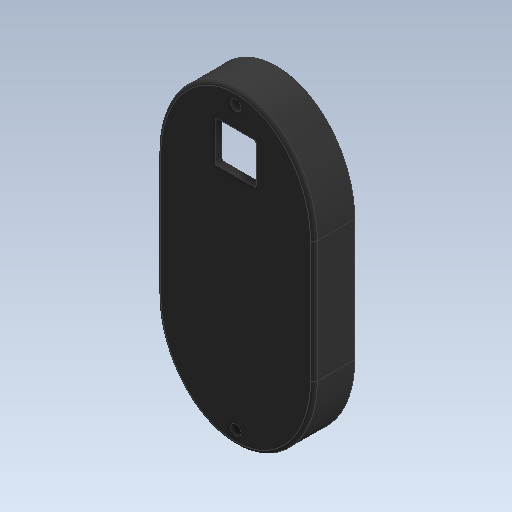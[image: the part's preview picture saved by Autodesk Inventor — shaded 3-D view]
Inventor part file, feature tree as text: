
AUTODESK INVENTOR PART (.ipt)
format: ipt  version: 2020 (Build 240168000, 168)  size: 245,760 bytes
history: native  units: mm
features: sketch x6, extrude x5, other x3, fillet x2, reference x2, projected_geometry x2, hole x1
ambient origin geometry x8: Origin, YZ Plane, XZ Plane, XY Plane, X Axis, Y Axis, Z Axis, Center Point
bodies: Solid1 (feature_tree)
feature tree (21):
  extrude  "Extrusion1"  Depth=10.0mm
  extrude  "Extrusion2"  Depth=10.0mm TaperAngle=0.0deg
  extrude  "Extrusion3"  Depth=8.0mm
  extrude  "Extrusion4"  Depth=10.0mm
  fillet  "Fillet1"  Radius=12.0mm
  hole  "Hole1"  [1 undecoded]
  extrude  "Extrusion5"  Depth=1.0mm
  fillet  "Fillet2"  Radius=10.0mm
  sketch  "Sketch1"  dims[d0=10.0mm d1=0.0mm d2=3.0mm]
  reference  "Reference1"
  reference  "Reference2"
  sketch  "Sketch2"  dims[d3=10.0mm d4=0.0mm d5=2.0mm d6=0.0mm]
  projected_geometry  "Projected Loop1"
  sketch  "Sketch3"  dims[d7=8.0mm d8=8.0mm]
  projected_geometry  "Projected Loop2"
  sketch  "Sketch4"  dims[d9=10.0mm d10=0.0mm d11=2.0mm]
  sketch  "Sketch5"  dims[d12=3.0mm d13=6.0mm d14=6.0mm d15=50.0mm d16=90.0deg d17=8.0mm d18=20.594885mm d19=12.0mm]
  sketch  "Sketch6"  dims[d20=12.0mm d21=0.5mm d22=6.0mm d23=10.0mm d24=0.0mm d25=1.0mm]
  other  "<userpath>\Documents\GitHub\OpenRaman\Hardware\OpenRaman.V1.iam"
  other  "OpenRaman.V1.iam"
  other  "PrismSensorHolder:1"
note: 1 required parameter value undecoded (feature->parameter linkage not recoverable at this tier; creation-order binding heuristic only, values carry confidence <= 0.55)
